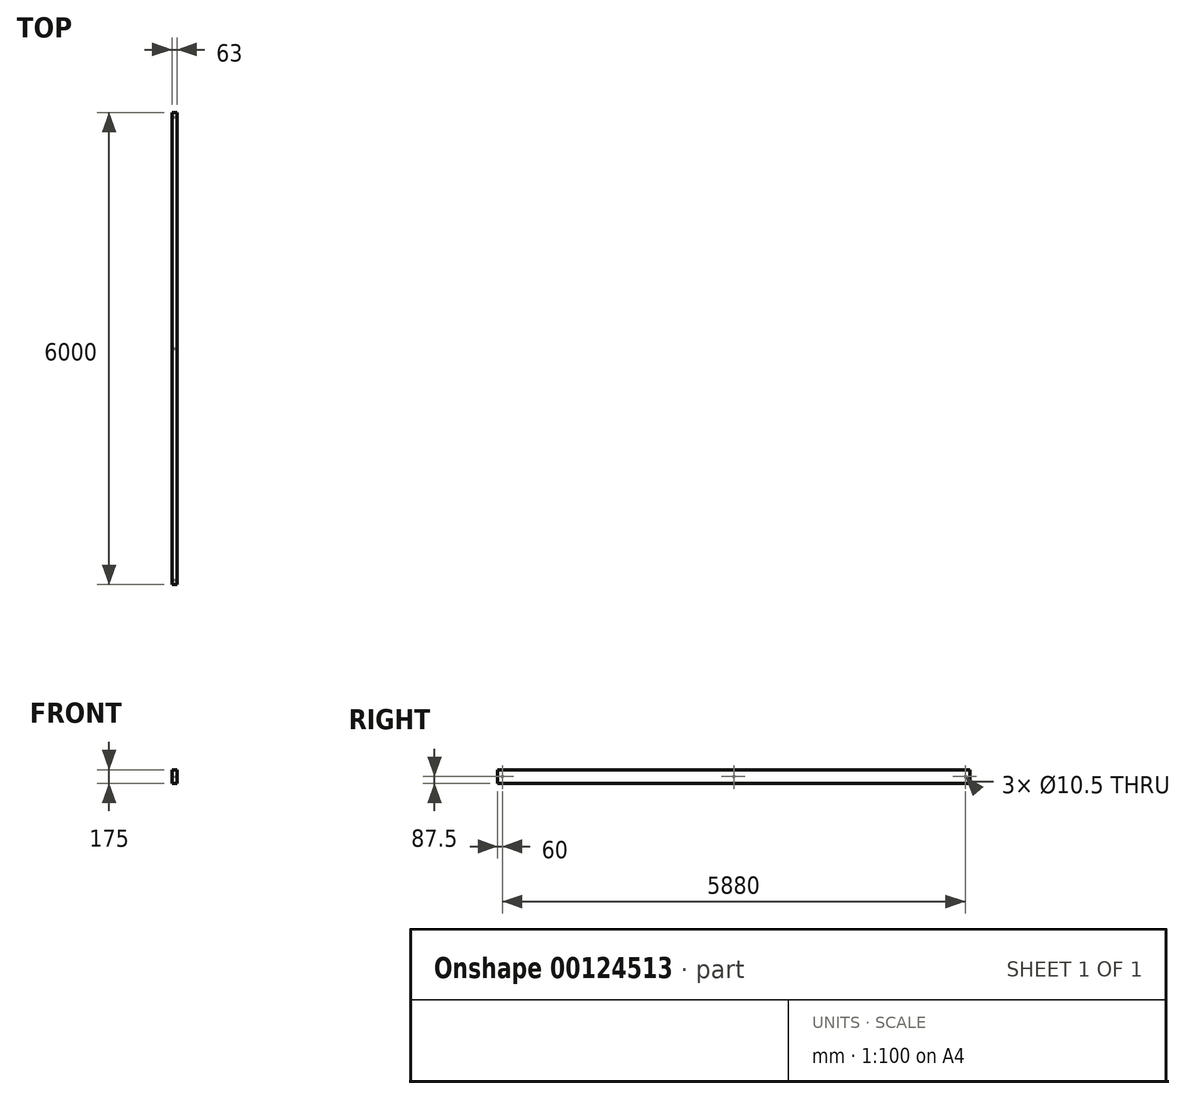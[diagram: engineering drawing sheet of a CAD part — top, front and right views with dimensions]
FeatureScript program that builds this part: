
annotation { "Feature Type Name" : "Feature", "Feature Type Description" : "" }
export const myFeature = defineFeature(function(context is Context, id is Id, definition is map)
    precondition{}
    {
        {
            var Q0;
            Q0=qCreatedBy(makeId("Front.planeOp"),FACE);
            var sketch = newSketch(context, id + "F0", { "sketchPlane" : qUnion([Q0])});
            skLineSegment(sketch, "E0.bottom", {"start": v(31.5, 87.5) * mm, "end": v(-31.5, 87.5) * mm});
            skLineSegment(sketch, "E0.top", {"start": v(31.5, -87.5) * mm, "end": v(-31.5, -87.5) * mm});
            skLineSegment(sketch, "E0.left", {"start": v(31.5, 87.5) * mm, "end": v(31.5, -87.5) * mm});
            skLineSegment(sketch, "E0.right", {"start": v(-31.5, 87.5) * mm, "end": v(-31.5, -87.5) * mm});
            skPoint(sketch, "E0.middle", {"position": v(0, 0) * mm});
            skSolve(sketch);
        }
        {
            var Q0;
            Q0 = qSketchRegion(id + "F0", true);
            extrude(context, id + "F1", {"entities" : qUnion([Q0]), "endBound" : BoundingType.SYMMETRIC, "depth" : 6000 * mm});
        }
        {
            var Q0;
            Q0=makeQuery(id+"F1.opExtrude","SWEPT_FACE",FACE,{"disambiguationData":[OSD([sQuery(id+"F0.wireOp",EDGE,"E0.left")])]});
            var sketch = newSketch(context, id + "F2", { "sketchPlane" : qUnion([Q0])});
            skCircle(sketch, "E1", {"center": v(-2940, 0) * mm, "radius": 5.25 * mm});
            skCircle(sketch, "E2", {"center": v(2940, 0) * mm, "radius": 5.25 * mm});
            skCircle(sketch, "E3", {"center": v(0, 0) * mm, "radius": 5.25 * mm});
            skSolve(sketch);
        }
        {
            var Q0;
            Q0 = qSketchRegion(id + "F2", true);
            extrude(context, id + "F3", {"entities" : qUnion([Q0]), "operationType" : NewBodyOperationType.REMOVE, "endBound" : BoundingType.THROUGH_ALL, "oppositeDirection" : true, "depth" : 25 * mm});
        }
    });
